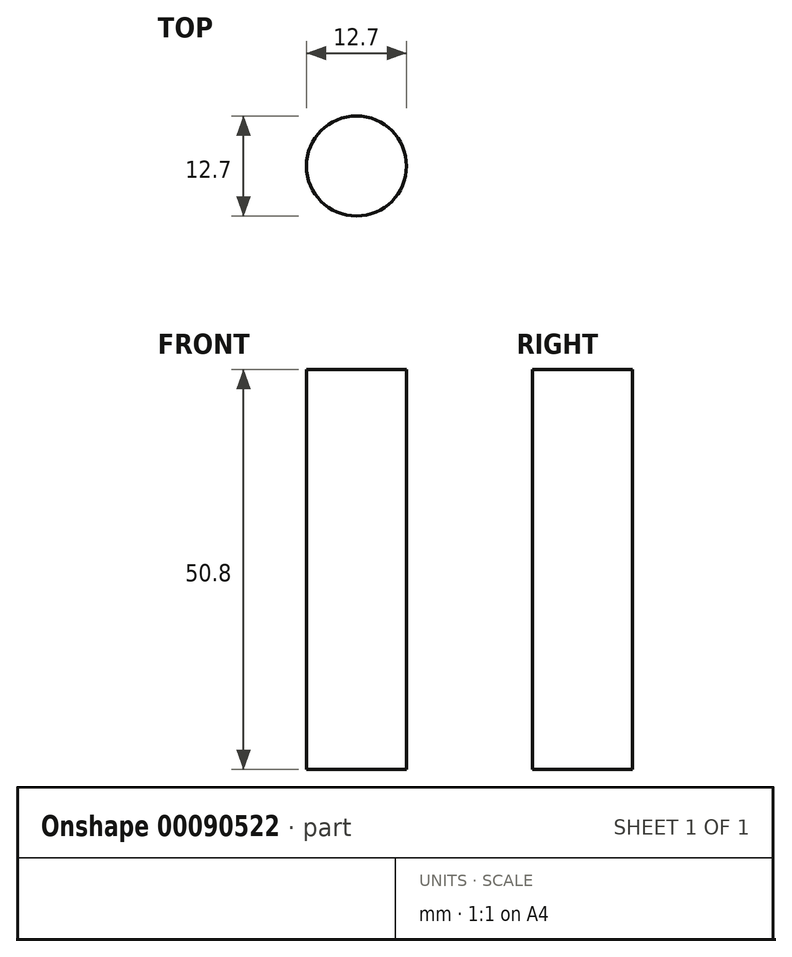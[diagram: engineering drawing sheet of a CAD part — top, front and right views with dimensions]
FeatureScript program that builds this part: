
annotation { "Feature Type Name" : "Feature", "Feature Type Description" : "" }
export const myFeature = defineFeature(function(context is Context, id is Id, definition is map)
    precondition{}
    {
        {
            var Q0;
            Q0=qCreatedBy(makeId("Top.planeOp"),FACE);
            var sketch = newSketch(context, id + "F0", { "sketchPlane" : qUnion([Q0])});
            skCircle(sketch, "E0", {"center": v(-62.07, 15.1) * mm, "radius": 6.35 * mm});
            skSolve(sketch);
        }
        {
            var Q0;
            Q0=makeQuery(id+"F0.imprint","IMPRINT",FACE,{"disambiguationData":[TD([[makeQuery(id+"F0.imprint","IMPRINT",EDGE,{"derivedFrom":sQuery(id+"F0.wireOp",EDGE,"E0")}),1.0]])]});
            extrude(context, id + "F1", {"entities" : qUnion([Q0]), "depth" : 50.8 * mm});
        }
    });
